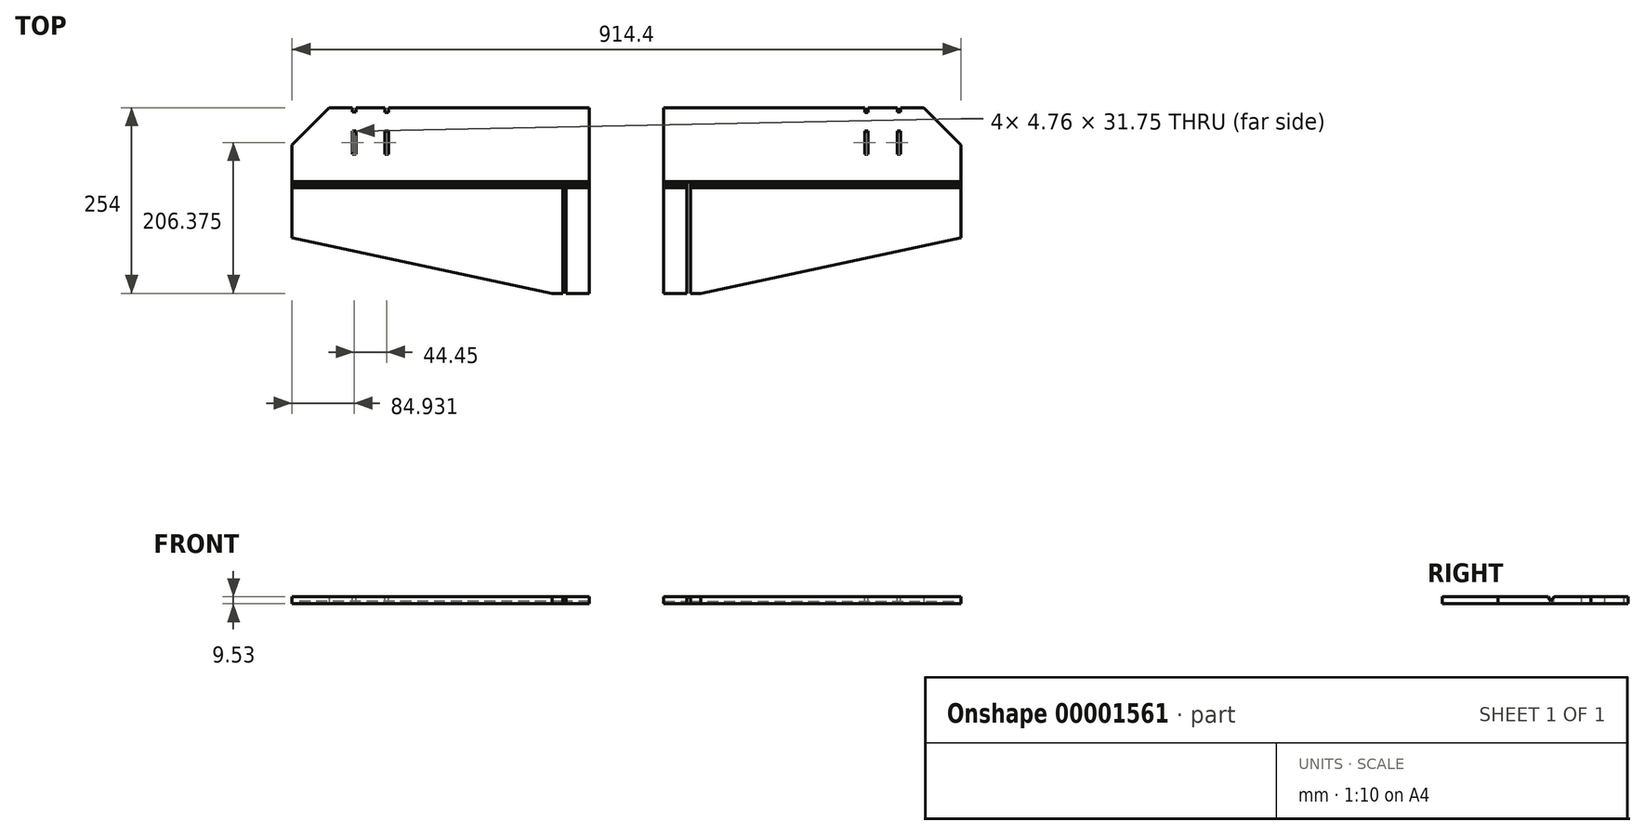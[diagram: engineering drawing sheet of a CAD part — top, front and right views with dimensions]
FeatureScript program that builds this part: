
annotation { "Feature Type Name" : "Feature", "Feature Type Description" : "" }
export const myFeature = defineFeature(function(context is Context, id is Id, definition is map)
    precondition{}
    {
        {
            var Q0;
            Q0=qCreatedBy(makeId("Top.planeOp"),FACE);
            var sketch = newSketch(context, id + "F0", { "sketchPlane" : qUnion([Q0])});
            skLineSegment(sketch, "E0", {"start": v(0, 0) * mm, "end": v(50.8, 0) * mm});
            skLineSegment(sketch, "E1", {"start": v(50.8, 0) * mm, "end": v(406.4, 76.28) * mm});
            skLineSegment(sketch, "E2", {"start": v(406.4, 76.28) * mm, "end": v(406.4, 203.28) * mm});
            skLineSegment(sketch, "E3", {"start": v(406.4, 203.28) * mm, "end": v(355.6, 254) * mm});
            skLineSegment(sketch, "E4", {"start": v(355.6, 254) * mm, "end": v(0, 254) * mm});
            skLineSegment(sketch, "E5", {"start": v(0, 254) * mm, "end": v(0, 0) * mm});
            skSolve(sketch);
        }
        {
            var Q0;
            Q0=makeQuery(id+"F0.imprint","IMPRINT",FACE,{"disambiguationData":[TD([[makeQuery(id+"F0.imprint","IMPRINT",EDGE,{"derivedFrom":sQuery(id+"F0.wireOp",EDGE,"E0")}),1.0]])]});
            extrude(context, id + "F1", {"entities" : qUnion([Q0]), "depth" : 9.52 * mm});
        }
        {
            var Q0;
            Q0=qCreatedBy(makeId("Top.planeOp"),FACE);
            var sketch = newSketch(context, id + "F2", { "sketchPlane" : qUnion([Q0])});
            skLineSegment(sketch, "E6", {"start": v(36.43, 0) * mm, "end": v(36.43, 152.4) * mm});
            skLineSegment(sketch, "E7", {"start": v(36.43, 152.4) * mm, "end": v(31.67, 152.4) * mm});
            skLineSegment(sketch, "E8", {"start": v(31.67, 152.4) * mm, "end": v(31.67, 0) * mm});
            skLineSegment(sketch, "E9", {"start": v(31.67, 0) * mm, "end": v(36.43, 0) * mm});
            skSolve(sketch);
        }
        {
            var Q0;
            Q0 = qSketchRegion(id + "F2", true);
            extrude(context, id + "F3", {"entities" : qUnion([Q0]), "operationType" : NewBodyOperationType.REMOVE, "endBound" : BoundingType.SYMMETRIC, "oppositeDirection" : true, "depth" : 25.4 * mm});
        }
        {
            var Q0;
            Q0=makeQuery(id+"F1.opExtrude","SWEPT_FACE",FACE,{"disambiguationData":[OSD([sQuery(id+"F0.wireOp",EDGE,"E2")])]});
            var sketch = newSketch(context, id + "F4", { "sketchPlane" : qUnion([Q0])});
            skLineSegment(sketch, "E10", {"start": v(144.54, 9.52) * mm, "end": v(148.56, 3.05) * mm});
            skLineSegment(sketch, "E11", {"start": v(148.56, 3.05) * mm, "end": v(152.58, 9.52) * mm});
            skSolve(sketch);
        }
        {
            var Q0;
            {var subQ2=sQuery(id+"F4.wireOp",EDGE,"E10");Q0=makeQuery(id+"F4.imprint","IMPRINT",FACE,{"disambiguationData":[TD([[makeQuery(id+"F4.imprint","IMPRINT",EDGE,{"derivedFrom":subQ2}),1.0]])]});}
            extrude(context, id + "F5", {"entities" : qUnion([Q0]), "operationType" : NewBodyOperationType.REMOVE, "oppositeDirection" : true, "depth" : 420.88 * mm});
        }
        {
            var Q0;
            {var subQ0=sQuery(id+"F0.wireOp",EDGE,"E0");var subQ1=sQuery(id+"F0.wireOp",EDGE,"E2");var subQ2=sQuery(id+"F0.wireOp",EDGE,"E3");var subQ3=sQuery(id+"F0.wireOp",EDGE,"E4");var subQ4=sQuery(id+"F0.wireOp",EDGE,"E5");Q0=makeQuery(id+"F5.boolean.opBoolean","SPLIT",FACE,{"disambiguationData":[TD([makeQuery(id+"F1.opExtrude","SWEPT_FACE",FACE,{"disambiguationData":[OSD([subQ2])]})])],"derivedFrom":makeQuery(id+"F1.opExtrude","CAP_FACE",FACE,{"disambiguationData":[OSD([subQ0,sQuery(id+"F0.wireOp",EDGE,"E1"),subQ1,subQ2,subQ3,subQ4])],"isStart":false})});}
            var sketch = newSketch(context, id + "F6", { "sketchPlane" : qUnion([Q0])});
            skLineSegment(sketch, "E12.bottom", {"start": v(319.09, 222.25) * mm, "end": v(323.85, 222.25) * mm});
            skLineSegment(sketch, "E12.top", {"start": v(319.09, 190.5) * mm, "end": v(323.85, 190.5) * mm});
            skLineSegment(sketch, "E12.left", {"start": v(319.09, 222.25) * mm, "end": v(319.09, 190.5) * mm});
            skLineSegment(sketch, "E12.right", {"start": v(323.85, 222.25) * mm, "end": v(323.85, 190.5) * mm});
            skSolve(sketch);
        }
        {
            var Q0;
            Q0=makeQuery(id+"F6.imprint","IMPRINT",FACE,{"disambiguationData":[TD([[makeQuery(id+"F6.imprint","IMPRINT",EDGE,{"derivedFrom":sQuery(id+"F6.wireOp",EDGE,"E12.bottom")}),-1.0]])]});
            extrude(context, id + "F7", {"entities" : qUnion([Q0]), "operationType" : NewBodyOperationType.REMOVE, "oppositeDirection" : true, "depth" : 25.4 * mm});
        }
        {
            var Q0;
            Q0=qCreatedBy(makeId("Top.planeOp"),FACE);
            var sketch = newSketch(context, id + "F8", { "sketchPlane" : qUnion([Q0])});
            skLineSegment(sketch, "E13.bottom", {"start": v(274.64, 222.25) * mm, "end": v(279.4, 222.25) * mm});
            skLineSegment(sketch, "E13.top", {"start": v(274.64, 190.5) * mm, "end": v(279.4, 190.5) * mm});
            skLineSegment(sketch, "E13.left", {"start": v(274.64, 222.25) * mm, "end": v(274.64, 190.5) * mm});
            skLineSegment(sketch, "E13.right", {"start": v(279.4, 222.25) * mm, "end": v(279.4, 190.5) * mm});
            skSolve(sketch);
        }
        {
            var Q0;
            Q0 = qSketchRegion(id + "F8", true);
            extrude(context, id + "F9", {"entities" : qUnion([Q0]), "operationType" : NewBodyOperationType.REMOVE, "endBound" : BoundingType.THROUGH_ALL, "depth" : 25.4 * mm});
        }
        {
            var Q0;
            Q0=qCreatedBy(makeId("Top.planeOp"),FACE);
            var sketch = newSketch(context, id + "F10", { "sketchPlane" : qUnion([Q0])});
            skLineSegment(sketch, "E14.bottom", {"start": v(319.1, 254.15) * mm, "end": v(323.85, 254.15) * mm});
            skLineSegment(sketch, "E14.top", {"start": v(319.1, 247.8) * mm, "end": v(323.85, 247.8) * mm});
            skLineSegment(sketch, "E14.left", {"start": v(319.1, 254.15) * mm, "end": v(319.1, 247.8) * mm});
            skLineSegment(sketch, "E14.right", {"start": v(323.85, 254.15) * mm, "end": v(323.85, 247.8) * mm});
            skSolve(sketch);
        }
        {
            var Q0;
            Q0 = qSketchRegion(id + "F10", true);
            extrude(context, id + "F11", {"entities" : qUnion([Q0]), "operationType" : NewBodyOperationType.REMOVE, "endBound" : BoundingType.THROUGH_ALL, "depth" : 25.4 * mm});
        }
        {
            var Q0;
            Q0=qCreatedBy(makeId("Top.planeOp"),FACE);
            var sketch = newSketch(context, id + "F12", { "sketchPlane" : qUnion([Q0])});
            skLineSegment(sketch, "E15.bottom", {"start": v(274.64, 254.04) * mm, "end": v(279.4, 254.04) * mm});
            skLineSegment(sketch, "E15.top", {"start": v(274.64, 247.7) * mm, "end": v(279.4, 247.7) * mm});
            skLineSegment(sketch, "E15.left", {"start": v(274.64, 254.04) * mm, "end": v(274.64, 247.7) * mm});
            skLineSegment(sketch, "E15.right", {"start": v(279.4, 254.04) * mm, "end": v(279.4, 247.7) * mm});
            skSolve(sketch);
        }
        {
            var Q0;
            Q0 = qSketchRegion(id + "F12", true);
            extrude(context, id + "F13", {"entities" : qUnion([Q0]), "operationType" : NewBodyOperationType.REMOVE, "endBound" : BoundingType.THROUGH_ALL, "depth" : 25.4 * mm});
        }
        {
            var Q0;
            Q0=qCreatedBy(makeId("Right.planeOp"),FACE);
            cPlane(context, id + "F14", {"entities" : qUnion([Q0]), "cplaneType" : CPlaneType.OFFSET, "offset" : 50.8 * mm, "oppositeDirection" : true, "width" : 152.4 * mm, "height" : 152.4 * mm});
        }
        {
            var Q0;
            Q0=makeQuery(id+"F1.opExtrude","SWEPT_BODY",BODY,{"disambiguationData":[OSD([sQuery(id+"F0.wireOp",EDGE,"E0"),sQuery(id+"F0.wireOp",EDGE,"E1"),sQuery(id+"F0.wireOp",EDGE,"E2"),sQuery(id+"F0.wireOp",EDGE,"E3"),sQuery(id+"F0.wireOp",EDGE,"E4"),sQuery(id+"F0.wireOp",EDGE,"E5")])]});
            var Q1;
            Q1=qCreatedBy(id+"F14.planeOp",FACE);
            mirror(context, id + "F15", {"entities" : qUnion([Q0]), "mirrorPlane" : qUnion([Q1])});
        }
    });
